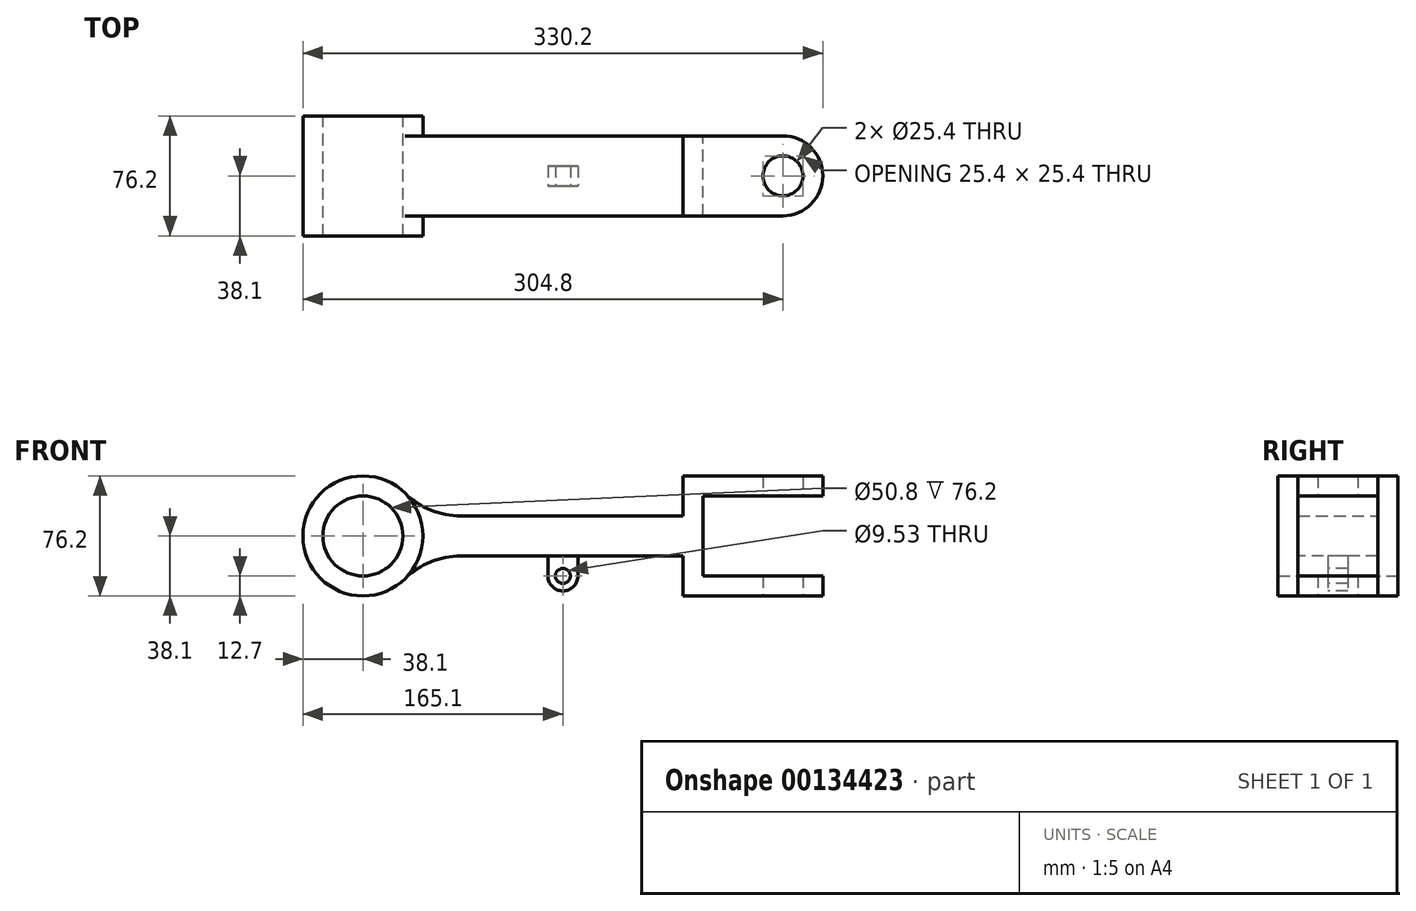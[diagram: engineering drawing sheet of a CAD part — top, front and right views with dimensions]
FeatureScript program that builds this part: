
annotation { "Feature Type Name" : "Feature", "Feature Type Description" : "" }
export const myFeature = defineFeature(function(context is Context, id is Id, definition is map)
    precondition{}
    {
        {
            var Q0;
            Q0=qCreatedBy(makeId("Front.planeOp"),FACE);
            var sketch = newSketch(context, id + "F0", { "sketchPlane" : qUnion([Q0])});
            skCircle(sketch, "E0", {"center": v(0, 0) * mm, "radius": 25.4 * mm});
            skCircle(sketch, "E1", {"center": v(0, 0) * mm, "radius": 38.1 * mm});
            skLineSegment(sketch, "E2", {"start": v(0, 0) * mm, "end": v(203.2, 0) * mm, "construction": true});
            skLineSegment(sketch, "E3.0", {"start": v(35.92, 12.7) * mm, "end": v(203.2, 12.7) * mm});
            skLineSegment(sketch, "E4", {"start": v(203.2, 0) * mm, "end": v(203.2, 38.1) * mm});
            skLineSegment(sketch, "E5", {"start": v(203.2, 38.1) * mm, "end": v(266.7, 38.1) * mm});
            skLineSegment(sketch, "E6", {"start": v(266.7, 38.1) * mm, "end": v(266.7, 25.4) * mm});
            skLineSegment(sketch, "E7", {"start": v(266.7, 25.4) * mm, "end": v(215.9, 25.4) * mm});
            skLineSegment(sketch, "E8", {"start": v(215.9, 25.4) * mm, "end": v(215.9, -25.4) * mm});
            skLineSegment(sketch, "E9", {"start": v(215.9, -25.4) * mm, "end": v(266.7, -25.4) * mm});
            skLineSegment(sketch, "E10", {"start": v(266.7, -25.4) * mm, "end": v(266.7, -38.1) * mm});
            skLineSegment(sketch, "E11", {"start": v(266.7, -38.1) * mm, "end": v(203.2, -38.1) * mm});
            skLineSegment(sketch, "E12", {"start": v(203.2, 0) * mm, "end": v(203.2, -38.1) * mm});
            skLineSegment(sketch, "E13.0", {"start": v(0, -12.7) * mm, "end": v(22, -12.7) * mm, "construction": true});
            skLineSegment(sketch, "E14.trimOffspring", {"start": v(35.92, -12.7) * mm, "end": v(203.2, -12.7) * mm});
            skSolve(sketch);
        }
        {
            var Q0;
            Q0 = qSketchRegion(id + "F0", true);
            var Q1;
            Q1=makeQuery(id+"F0.imprint","IMPRINT",FACE,{"disambiguationData":[TD([[makeQuery(id+"F0.imprint","IMPRINT",EDGE,{"derivedFrom":sQuery(id+"F0.wireOp",EDGE,"E0")}),-1.0]])]});
            var Q2;
            {var subQ4=sQuery(id+"F0.wireOp",EDGE,"E3.0");Q2=makeQuery(id+"F0.imprint","IMPRINT",FACE,{"disambiguationData":[TD([[makeQuery(id+"F0.imprint","IMPRINT",EDGE,{"derivedFrom":subQ4}),-1.0]])]});}
            var Q3;
            {var subQ5=sQuery(id+"F0.wireOp",EDGE,"E5");Q3=makeQuery(id+"F0.imprint","IMPRINT",FACE,{"disambiguationData":[TD([[makeQuery(id+"F0.imprint","IMPRINT",EDGE,{"derivedFrom":subQ5}),-1.0]])]});}
            extrude(context, id + "F1", {"entities" : qUnion([Q0, Q1, Q2, Q3]), "depth" : 50.8 * mm});
        }
        {
            var Q0;
            Q0=makeQuery(id+"F1.opExtrude","CAP_FACE",FACE,{"disambiguationData":[OSD([sQuery(id+"F0.wireOp",EDGE,"E0"),sQuery(id+"F0.wireOp",EDGE,"E1"),sQuery(id+"F0.wireOp",EDGE,"E3.0"),sQuery(id+"F0.wireOp",EDGE,"E4"),sQuery(id+"F0.wireOp",EDGE,"E5"),sQuery(id+"F0.wireOp",EDGE,"E6"),sQuery(id+"F0.wireOp",EDGE,"E7"),sQuery(id+"F0.wireOp",EDGE,"E8"),sQuery(id+"F0.wireOp",EDGE,"E9"),sQuery(id+"F0.wireOp",EDGE,"E10"),sQuery(id+"F0.wireOp",EDGE,"E11"),sQuery(id+"F0.wireOp",EDGE,"E12"),sQuery(id+"F0.wireOp",EDGE,"E14.trimOffspring")])],"isStart":false});
            var sketch = newSketch(context, id + "F2", { "sketchPlane" : qUnion([Q0])});
            skCircle(sketch, "E15", {"center": v(0, 0) * mm, "radius": 25.4 * mm});
            skCircle(sketch, "E16", {"center": v(0, 0) * mm, "radius": 38.1 * mm});
            skSolve(sketch);
        }
        {
            var Q0;
            Q0 = qSketchRegion(id + "F2", true);
            var Q1;
            Q1 = qSketchRegion(id + "F9", true);
            extrude(context, id + "F3", {"entities" : qUnion([Q0, Q1]), "operationType" : NewBodyOperationType.ADD, "depth" : 12.7 * mm});
        }
        {
            var Q0;
            Q0=makeQuery(id+"F1.opExtrude","CAP_FACE",FACE,{"disambiguationData":[OSD([sQuery(id+"F0.wireOp",EDGE,"E0"),sQuery(id+"F0.wireOp",EDGE,"E1"),sQuery(id+"F0.wireOp",EDGE,"E3.0"),sQuery(id+"F0.wireOp",EDGE,"E4"),sQuery(id+"F0.wireOp",EDGE,"E5"),sQuery(id+"F0.wireOp",EDGE,"E6"),sQuery(id+"F0.wireOp",EDGE,"E7"),sQuery(id+"F0.wireOp",EDGE,"E8"),sQuery(id+"F0.wireOp",EDGE,"E9"),sQuery(id+"F0.wireOp",EDGE,"E10"),sQuery(id+"F0.wireOp",EDGE,"E11"),sQuery(id+"F0.wireOp",EDGE,"E12"),sQuery(id+"F0.wireOp",EDGE,"E14.trimOffspring")])],"isStart":true});
            var sketch = newSketch(context, id + "F4", { "sketchPlane" : qUnion([Q0])});
            skCircle(sketch, "E17", {"center": v(0, 0) * mm, "radius": 25.4 * mm});
            skCircle(sketch, "E18", {"center": v(0, 0) * mm, "radius": 38.1 * mm});
            skSolve(sketch);
        }
        {
            var Q0;
            Q0 = qSketchRegion(id + "F4", true);
            extrude(context, id + "F5", {"entities" : qUnion([Q0]), "operationType" : NewBodyOperationType.ADD, "depth" : 12.7 * mm});
        }
        {
            var Q0;
            Q0=makeQuery(id+"F1.opExtrude","SWEPT_EDGE",EDGE,{"disambiguationData":[OSD([sQuery(id+"F0.wireOp",EDGE,"E1"),sQuery(id+"F0.wireOp",EDGE,"E14.trimOffspring")])]});
            var Q1;
            Q1=makeQuery(id+"F1.opExtrude","SWEPT_EDGE",EDGE,{"disambiguationData":[OSD([sQuery(id+"F0.wireOp",EDGE,"E1"),sQuery(id+"F0.wireOp",EDGE,"E3.0")])]});
            fillet(context, id + "F6", {"entities" : qUnion([Q0, Q1]), "radius" : 50.8 * mm, "tangentPropagation" : true, "allowEdgeOverflow" : false});
        }
        {
            var Q0;
            Q0=makeQuery(id+"F1.opExtrude","SWEPT_FACE",FACE,{"disambiguationData":[OSD([sQuery(id+"F0.wireOp",EDGE,"E11")])]});
            var sketch = newSketch(context, id + "F7", { "sketchPlane" : qUnion([Q0])});
            skArc(sketch, "E19", {"start": v(266.7, 0) * mm, "mid": v(292.1, 25.4) * mm, "end": v(266.7, 50.8) * mm});
            skCircle(sketch, "E20", {"center": v(266.7, 25.4) * mm, "radius": 12.7 * mm});
            skSolve(sketch);
        }
        {
            var Q0;
            Q0 = qSketchRegion(id + "F7", true);
            var Q1;
            Q1=makeQuery(id+"F7.imprint","IMPRINT",FACE,{"disambiguationData":[TD([[makeQuery(id+"F7.imprint","IMPRINT",EDGE,{"derivedFrom":sQuery(id+"F7.wireOp",EDGE,"E19")}),1.0]])]});
            extrude(context, id + "F8", {"entities" : qUnion([Q0, Q1]), "operationType" : NewBodyOperationType.ADD, "oppositeDirection" : true, "depth" : 12.7 * mm});
        }
        {
            var Q0;
            Q0=makeQuery(id+"F1.opExtrude","SWEPT_FACE",FACE,{"disambiguationData":[OSD([sQuery(id+"F0.wireOp",EDGE,"E5")])]});
            var sketch = newSketch(context, id + "F9", { "sketchPlane" : qUnion([Q0])});
            skArc(sketch, "E21", {"start": v(266.7, -50.8) * mm, "mid": v(292.1, -25.4) * mm, "end": v(266.7, 0) * mm});
            skSolve(sketch);
        }
        {
            var Q0;
            Q0=makeQuery(id+"F9.imprint","IMPRINT",FACE,{"disambiguationData":[TD([[makeQuery(id+"F9.imprint","IMPRINT",EDGE,{"derivedFrom":sQuery(id+"F9.wireOp",EDGE,"E21")}),1.0]])]});
            extrude(context, id + "F10", {"entities" : qUnion([Q0]), "operationType" : NewBodyOperationType.ADD, "oppositeDirection" : true, "depth" : 12.7 * mm});
        }
        {
            var Q0;
            {var subQ0=sQuery(id+"F7.wireOp",EDGE,"E20");var subQ1=makeQuery(id+"F1.opExtrude","SWEPT_EDGE",EDGE,{"disambiguationData":[OSD([sQuery(id+"F0.wireOp",EDGE,"E10"),sQuery(id+"F0.wireOp",EDGE,"E11")])]});var subQ2=makeQuery(id+"F7.imprint","INTERSECT",VERTEX,{"disambiguationData":[OD(0.0)],"derivedFrom":[subQ1,subQ0]});Q0=makeQuery(id+"F7.imprint","IMPRINT",FACE,{"disambiguationData":[TD([[makeQuery(id+"F7.imprint","IMPRINT",EDGE,{"disambiguationData":[TD([[subQ2,-1.0]])],"derivedFrom":subQ0}),1.0]])]});}
            var Q1;
            {var subQ0=sQuery(id+"F7.wireOp",EDGE,"E20");var subQ1=makeQuery(id+"F1.opExtrude","SWEPT_EDGE",EDGE,{"disambiguationData":[OSD([sQuery(id+"F0.wireOp",EDGE,"E10"),sQuery(id+"F0.wireOp",EDGE,"E11")])]});var subQ2=makeQuery(id+"F7.imprint","INTERSECT",VERTEX,{"disambiguationData":[OD(0.0)],"derivedFrom":[subQ1,subQ0]});Q1=makeQuery(id+"F7.imprint","IMPRINT",FACE,{"disambiguationData":[TD([[makeQuery(id+"F7.imprint","IMPRINT",EDGE,{"disambiguationData":[TD([[subQ2,1.0]])],"derivedFrom":subQ0}),1.0]])]});}
            extrude(context, id + "F11", {"entities" : qUnion([Q0, Q1]), "operationType" : NewBodyOperationType.REMOVE, "endBound" : BoundingType.THROUGH_ALL, "oppositeDirection" : true, "depth" : 25.4 * mm});
        }
        {
            var Q0;
            Q0=makeQuery(id+"F1.opExtrude","CAP_FACE",FACE,{"disambiguationData":[OSD([sQuery(id+"F0.wireOp",EDGE,"E0"),sQuery(id+"F0.wireOp",EDGE,"E1"),sQuery(id+"F0.wireOp",EDGE,"E3.0"),sQuery(id+"F0.wireOp",EDGE,"E4"),sQuery(id+"F0.wireOp",EDGE,"E5"),sQuery(id+"F0.wireOp",EDGE,"E6"),sQuery(id+"F0.wireOp",EDGE,"E7"),sQuery(id+"F0.wireOp",EDGE,"E8"),sQuery(id+"F0.wireOp",EDGE,"E9"),sQuery(id+"F0.wireOp",EDGE,"E10"),sQuery(id+"F0.wireOp",EDGE,"E11"),sQuery(id+"F0.wireOp",EDGE,"E12"),sQuery(id+"F0.wireOp",EDGE,"E14.trimOffspring")])],"isStart":true});
            var Q1;
            Q1 = qBodyType(qCreatedBy(id + "F13" ,EDGE), BodyType.WIRE);
            cPlane(context, id + "F12", {"entities" : qUnion([Q0, Q1]), "cplaneType" : CPlaneType.OFFSET, "offset" : 25.4 * mm, "oppositeDirection" : true, "width" : 152.4 * mm, "height" : 152.4 * mm});
        }
        {
            var Q0;
            Q0=qCreatedBy(id+"F12.planeOp",FACE);
            var sketch = newSketch(context, id + "F13", { "sketchPlane" : qUnion([Q0])});
            skLineSegment(sketch, "E22.0", {"start": v(-62.22, -12.7) * mm, "end": v(-203.2, -12.7) * mm});
            skLineSegment(sketch, "E23.bottom", {"start": v(-136.53, -12.7) * mm, "end": v(-117.48, -12.7) * mm});
            skLineSegment(sketch, "E23.top", {"start": v(-136.53, -25.4) * mm, "end": v(-117.47, -25.4) * mm});
            skLineSegment(sketch, "E23.left", {"start": v(-136.53, -12.7) * mm, "end": v(-136.53, -25.4) * mm});
            skLineSegment(sketch, "E23.right", {"start": v(-117.48, -12.7) * mm, "end": v(-117.48, -25.4) * mm});
            skArc(sketch, "E24", {"start": v(-136.53, -25.4) * mm, "mid": v(-127, -34.92) * mm, "end": v(-117.47, -25.4) * mm});
            skCircle(sketch, "E25", {"center": v(-127, -25.4) * mm, "radius": 4.76 * mm});
            skSolve(sketch);
        }
        {
            var Q0;
            Q0 = qSketchRegion(id + "F13", true);
            extrude(context, id + "F14", {"entities" : qUnion([Q0]), "operationType" : NewBodyOperationType.ADD, "endBound" : BoundingType.SYMMETRIC, "depth" : 12.7 * mm});
        }
    });
